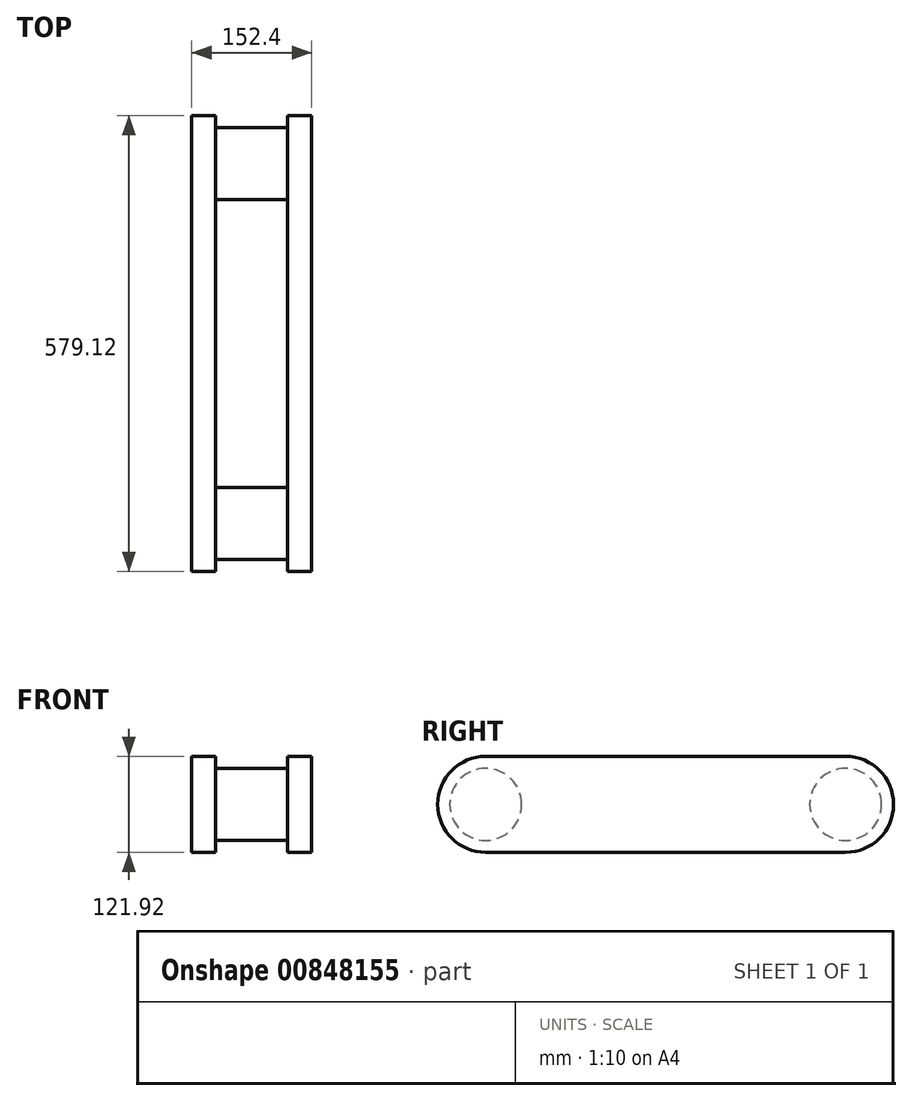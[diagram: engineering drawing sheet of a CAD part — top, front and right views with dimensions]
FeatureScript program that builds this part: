
annotation { "Feature Type Name" : "Feature", "Feature Type Description" : "" }
export const myFeature = defineFeature(function(context is Context, id is Id, definition is map)
    precondition{}
    {
        {
            var Q0;
            Q0=qCreatedBy(makeId("Right.planeOp"),FACE);
            var sketch = newSketch(context, id + "F0", { "sketchPlane" : qUnion([Q0])});
            skLineSegment(sketch, "E0.bottom", {"start": v(-228.6, 60.96) * mm, "end": v(228.6, 60.96) * mm});
            skLineSegment(sketch, "E0.top", {"start": v(-228.6, -60.96) * mm, "end": v(228.6, -60.96) * mm});
            skLineSegment(sketch, "E0.left", {"start": v(-228.6, 60.96) * mm, "end": v(-228.6, -60.96) * mm});
            skLineSegment(sketch, "E0.right", {"start": v(228.6, 60.96) * mm, "end": v(228.6, -60.96) * mm});
            skPoint(sketch, "E0.middle", {"position": v(0, 0) * mm});
            skCircle(sketch, "E1", {"center": v(-228.6, 0) * mm, "radius": 45.72 * mm});
            skCircle(sketch, "E2", {"center": v(228.6, 0) * mm, "radius": 45.72 * mm});
            skCircle(sketch, "E3", {"center": v(228.6, 0) * mm, "radius": 60.96 * mm});
            skCircle(sketch, "E4", {"center": v(-228.6, 0) * mm, "radius": 60.96 * mm});
            skSolve(sketch);
        }
        {
            var Q0;
            Q0 = qSketchRegion(id + "F0", true);
            var Q1;
            {var subQ0=sQuery(id+"F0.wireOp",EDGE,"E1");var subQ1=sQuery(id+"F0.wireOp",EDGE,"E0.left");var subQ2=makeQuery(id+"F0.imprint","INTERSECT",VERTEX,{"disambiguationData":[OD(0.0)],"derivedFrom":[subQ1,subQ0]});Q1=makeQuery(id+"F0.imprint","IMPRINT",FACE,{"disambiguationData":[TD([[makeQuery(id+"F0.imprint","IMPRINT",EDGE,{"disambiguationData":[TD([[subQ2,-1.0]])],"derivedFrom":subQ1}),-1.0]])]});}
            var Q2;
            {var subQ0=sQuery(id+"F0.wireOp",EDGE,"E1");var subQ1=sQuery(id+"F0.wireOp",EDGE,"E0.left");var subQ2=makeQuery(id+"F0.imprint","INTERSECT",VERTEX,{"disambiguationData":[OD(0.0)],"derivedFrom":[subQ1,subQ0]});Q2=makeQuery(id+"F0.imprint","IMPRINT",FACE,{"disambiguationData":[TD([[makeQuery(id+"F0.imprint","IMPRINT",EDGE,{"disambiguationData":[TD([[subQ2,-1.0]])],"derivedFrom":subQ1}),1.0]])]});}
            var Q3;
            {var subQ0=sQuery(id+"F0.wireOp",EDGE,"E2");var subQ1=sQuery(id+"F0.wireOp",EDGE,"E0.right");var subQ2=makeQuery(id+"F0.imprint","INTERSECT",VERTEX,{"disambiguationData":[OD(0.0)],"derivedFrom":[subQ1,subQ0]});Q3=makeQuery(id+"F0.imprint","IMPRINT",FACE,{"disambiguationData":[TD([[makeQuery(id+"F0.imprint","IMPRINT",EDGE,{"disambiguationData":[TD([[subQ2,-1.0]])],"derivedFrom":subQ1}),-1.0]])]});}
            var Q4;
            {var subQ0=sQuery(id+"F0.wireOp",EDGE,"E2");var subQ1=sQuery(id+"F0.wireOp",EDGE,"E0.right");var subQ2=makeQuery(id+"F0.imprint","INTERSECT",VERTEX,{"disambiguationData":[OD(0.0)],"derivedFrom":[subQ1,subQ0]});Q4=makeQuery(id+"F0.imprint","IMPRINT",FACE,{"disambiguationData":[TD([[makeQuery(id+"F0.imprint","IMPRINT",EDGE,{"disambiguationData":[TD([[subQ2,-1.0]])],"derivedFrom":subQ1}),1.0]])]});}
            extrude(context, id + "F1", {"entities" : qUnion([Q0, Q1, Q2, Q3, Q4]), "depth" : 152.4 * mm, "offsetDistance" : 30.48 * mm, "symmetric" : true});
        }
        {
            var Q0;
            {var subQ0=sQuery(id+"F0.wireOp",EDGE,"E0.bottom");Q0=makeQuery(id+"F0.imprint","IMPRINT",FACE,{"disambiguationData":[TD([[makeQuery(id+"F0.imprint","IMPRINT",EDGE,{"derivedFrom":subQ0}),-1.0]])]});}
            var Q1;
            {var subQ1=sQuery(id+"F0.wireOp",EDGE,"E0.left");var subQ3=sQuery(id+"F0.wireOp",EDGE,"E1");var subQ4=makeQuery(id+"F0.imprint","INTERSECT",VERTEX,{"disambiguationData":[OD(0.0)],"derivedFrom":[subQ1,subQ3]});Q1=makeQuery(id+"F0.imprint","IMPRINT",FACE,{"disambiguationData":[TD([[makeQuery(id+"F0.imprint","IMPRINT",EDGE,{"disambiguationData":[TD([[subQ4,1.0]])],"derivedFrom":subQ3}),-1.0]])]});}
            var Q2;
            {var subQ1=sQuery(id+"F0.wireOp",EDGE,"E0.left");var subQ3=sQuery(id+"F0.wireOp",EDGE,"E1");var subQ4=makeQuery(id+"F0.imprint","INTERSECT",VERTEX,{"disambiguationData":[OD(0.0)],"derivedFrom":[subQ1,subQ3]});Q2=makeQuery(id+"F0.imprint","IMPRINT",FACE,{"disambiguationData":[TD([[makeQuery(id+"F0.imprint","IMPRINT",EDGE,{"disambiguationData":[TD([[subQ4,-1.0]])],"derivedFrom":subQ3}),-1.0]])]});}
            var Q3;
            {var subQ1=sQuery(id+"F0.wireOp",EDGE,"E0.right");var subQ3=sQuery(id+"F0.wireOp",EDGE,"E2");var subQ4=makeQuery(id+"F0.imprint","INTERSECT",VERTEX,{"disambiguationData":[OD(0.0)],"derivedFrom":[subQ1,subQ3]});Q3=makeQuery(id+"F0.imprint","IMPRINT",FACE,{"disambiguationData":[TD([[makeQuery(id+"F0.imprint","IMPRINT",EDGE,{"disambiguationData":[TD([[subQ4,-1.0]])],"derivedFrom":subQ3}),-1.0]])]});}
            var Q4;
            {var subQ1=sQuery(id+"F0.wireOp",EDGE,"E0.right");var subQ3=sQuery(id+"F0.wireOp",EDGE,"E2");var subQ4=makeQuery(id+"F0.imprint","INTERSECT",VERTEX,{"disambiguationData":[OD(0.0)],"derivedFrom":[subQ1,subQ3]});Q4=makeQuery(id+"F0.imprint","IMPRINT",FACE,{"disambiguationData":[TD([[makeQuery(id+"F0.imprint","IMPRINT",EDGE,{"disambiguationData":[TD([[subQ4,1.0]])],"derivedFrom":subQ3}),-1.0]])]});}
            extrude(context, id + "F2", {"entities" : qUnion([Q0, Q1, Q2, Q3, Q4]), "operationType" : NewBodyOperationType.REMOVE, "depth" : 91.44 * mm, "offsetDistance" : 30.48 * mm, "symmetric" : true});
        }
    });
